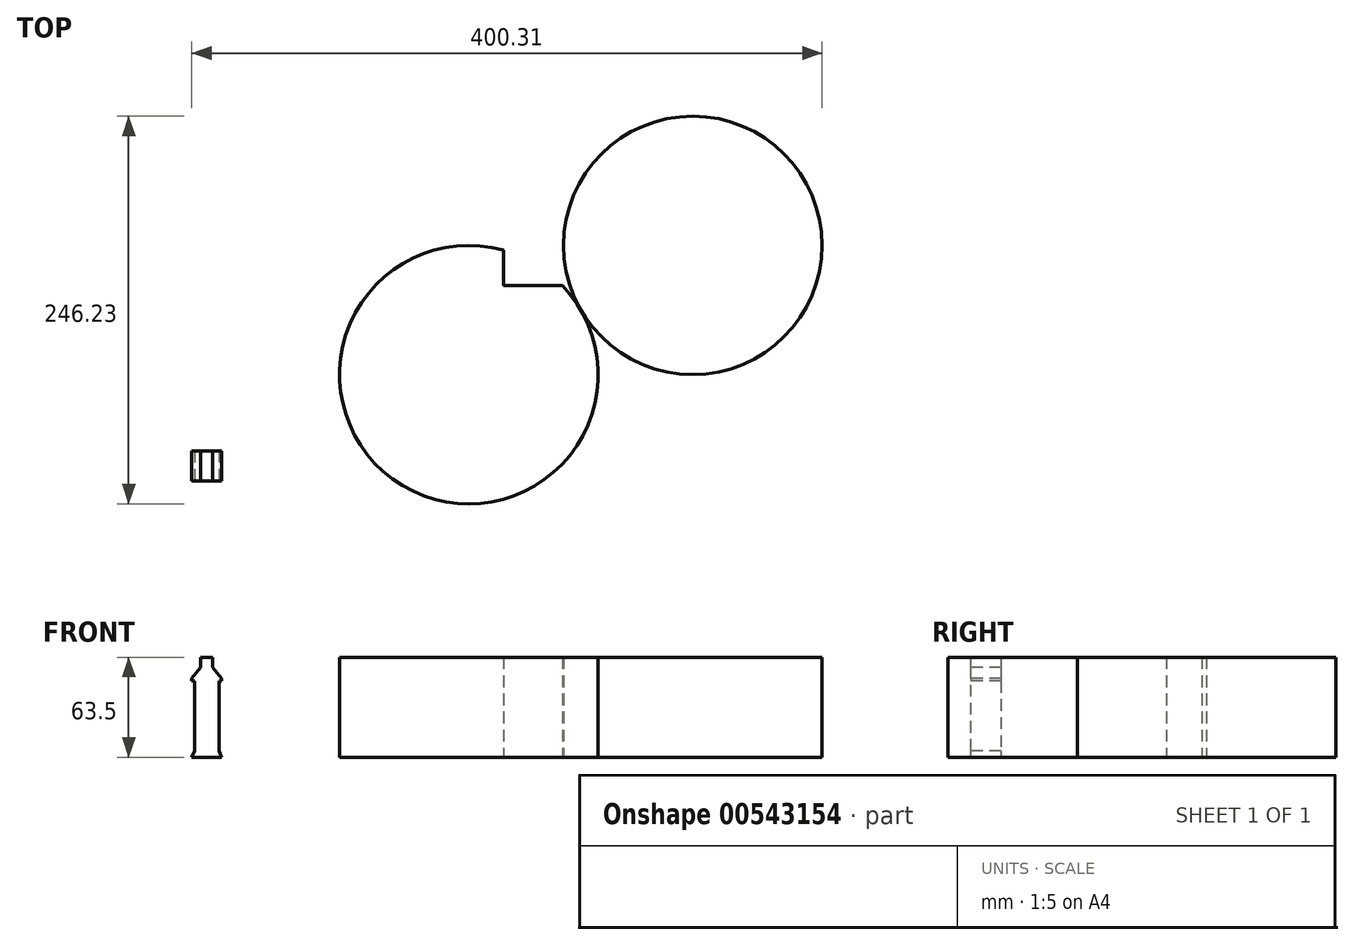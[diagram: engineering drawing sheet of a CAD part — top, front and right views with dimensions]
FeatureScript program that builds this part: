
annotation { "Feature Type Name" : "Feature", "Feature Type Description" : "" }
export const myFeature = defineFeature(function(context is Context, id is Id, definition is map)
    precondition{}
    {
        {
            var Q0;
            Q0=qCreatedBy(makeId("Top.planeOp"),FACE);
            var sketch = newSketch(context, id + "F0", { "sketchPlane" : qUnion([Q0])});
            skCircle(sketch, "E0", {"center": v(0, 0) * mm, "radius": 82.08 * mm});
            skCircle(sketch, "E1", {"center": v(0, 164.15) * mm, "radius": 82.08 * mm});
            skCircle(sketch, "E2", {"center": v(142.26, 82.08) * mm, "radius": 82.08 * mm});
            skPoint(sketch, "E3.startSnap0", {"position": v(71.13, 41.04) * mm});
            skLineSegment(sketch, "E4.bottom", {"start": v(21.96, 107.48) * mm, "end": v(72.76, 107.48) * mm});
            skLineSegment(sketch, "E4.top", {"start": v(21.96, 56.68) * mm, "end": v(72.76, 56.68) * mm});
            skLineSegment(sketch, "E4.left", {"start": v(21.96, 107.48) * mm, "end": v(21.96, 56.68) * mm});
            skLineSegment(sketch, "E4.right", {"start": v(72.76, 107.48) * mm, "end": v(72.76, 56.68) * mm});
            skSolve(sketch);
        }
        {
            var Q0;
            {var subQ0=sQuery(id+"F0.wireOp",EDGE,"E2");var subQ1=makeQuery(id+"F0.imprint","INTERSECT",VERTEX,{"derivedFrom":[sQuery(id+"F0.wireOp",EDGE,"5Xh8nU1x-Kccz-F1XJ-XfT3-ni66cKLijJze"),subQ0]});Q0=makeQuery(id+"F0.imprint","IMPRINT",FACE,{"disambiguationData":[TD([[makeQuery(id+"F0.imprint","IMPRINT",EDGE,{"disambiguationData":[TD([[subQ1,1.0]])],"derivedFrom":subQ0}),1.0]])]});}
            var Q1;
            {var subQ0=sQuery(id+"F0.wireOp",EDGE,"rKZXuCPi-gWcS-8Nuf-9jpB-Da6s8gIS6jwx");var subQ3=sQuery(id+"F0.wireOp",EDGE,"E2");var subQ7=makeQuery(id+"F0.imprint","INTERSECT",VERTEX,{"derivedFrom":[subQ3,subQ0]});Q1=makeQuery(id+"F0.imprint","IMPRINT",FACE,{"disambiguationData":[TD([[makeQuery(id+"F0.imprint","IMPRINT",EDGE,{"disambiguationData":[TD([[subQ7,-1.0]])],"derivedFrom":subQ3}),1.0]])]});}
            var Q2;
            {var subQ0=sQuery(id+"F0.wireOp",EDGE,"gLqf2wn5-t1Jo-fTFw-Qeks-cKj9YftUuhbS");var subQ1=sQuery(id+"F0.wireOp",EDGE,"E2");var subQ3=makeQuery(id+"F0.imprint","INTERSECT",VERTEX,{"derivedFrom":[subQ1,subQ0]});Q2=makeQuery(id+"F0.imprint","IMPRINT",FACE,{"disambiguationData":[TD([[makeQuery(id+"F0.imprint","IMPRINT",EDGE,{"disambiguationData":[TD([[subQ3,-1.0]])],"derivedFrom":subQ1}),1.0]])]});}
            var Q3;
            {var subQ0=sQuery(id+"F0.wireOp",EDGE,"ui8SPNsS-ngPU-wNeO-te97-4uBNf3wigOtR");Q3=makeQuery(id+"F0.imprint","IMPRINT",FACE,{"disambiguationData":[TD([[makeQuery(id+"F0.imprint","IMPRINT",EDGE,{"derivedFrom":subQ0}),1.0]])]});}
            var Q4;
            {var subQ0=sQuery(id+"F0.wireOp",EDGE,"ui8SPNsS-ngPU-wNeO-te97-4uBNf3wigOtR");Q4=makeQuery(id+"F0.imprint","IMPRINT",FACE,{"disambiguationData":[TD([[makeQuery(id+"F0.imprint","IMPRINT",EDGE,{"derivedFrom":subQ0}),-1.0]])]});}
            var Q5;
            {var subQ0=sQuery(id+"F0.wireOp",EDGE,"4fa8Zo42-phiU-RVQB-DN5M-7mljlmKBfd5X");Q5=makeQuery(id+"F0.imprint","IMPRINT",FACE,{"disambiguationData":[TD([[makeQuery(id+"F0.imprint","IMPRINT",EDGE,{"derivedFrom":subQ0}),-1.0]])]});}
            var Q6;
            {var subQ0=sQuery(id+"F0.wireOp",EDGE,"E3");var subQ1=sQuery(id+"F0.wireOp",EDGE,"E0");var subQ3=makeQuery(id+"F0.imprint","INTERSECT",VERTEX,{"derivedFrom":[subQ1,subQ0]});Q6=makeQuery(id+"F0.imprint","IMPRINT",FACE,{"disambiguationData":[TD([[makeQuery(id+"F0.imprint","IMPRINT",EDGE,{"disambiguationData":[TD([[subQ3,-1.0]])],"derivedFrom":subQ1}),1.0]])]});}
            var Q7;
            {var subQ0=sQuery(id+"F0.wireOp",EDGE,"HXteInfV-cd6M-VXyz-XBM5-8RgosEx2xvVP");Q7=makeQuery(id+"F0.imprint","IMPRINT",FACE,{"disambiguationData":[TD([[makeQuery(id+"F0.imprint","IMPRINT",EDGE,{"derivedFrom":subQ0}),1.0]])]});}
            var Q8;
            {var subQ5=sQuery(id+"F0.wireOp",EDGE,"HXteInfV-cd6M-VXyz-XBM5-8RgosEx2xvVP");Q8=makeQuery(id+"F0.imprint","IMPRINT",FACE,{"disambiguationData":[TD([[makeQuery(id+"F0.imprint","IMPRINT",EDGE,{"derivedFrom":subQ5}),-1.0]])]});}
            var Q9;
            {var subQ0=sQuery(id+"F0.wireOp",EDGE,"5Xh8nU1x-Kccz-F1XJ-XfT3-ni66cKLijJze");var subQ1=sQuery(id+"F0.wireOp",EDGE,"E0");var subQ2=makeQuery(id+"F0.imprint","INTERSECT",VERTEX,{"derivedFrom":[subQ1,subQ0]});Q9=makeQuery(id+"F0.imprint","IMPRINT",FACE,{"disambiguationData":[TD([[makeQuery(id+"F0.imprint","IMPRINT",EDGE,{"disambiguationData":[TD([[subQ2,-1.0]])],"derivedFrom":subQ1}),1.0]])]});}
            extrude(context, id + "F1", {"entities" : qUnion([Q0, Q1, Q2, Q3, Q4, Q5, Q6, Q7, Q8, Q9]), "depth" : 63.5 * mm, "offsetDistance" : 25.4 * mm});
        }
        {
            var Q0;
            Q0=qCreatedBy(makeId("Top.planeOp"),FACE);
            var sketch = newSketch(context, id + "F2", { "sketchPlane" : qUnion([Q0])});
            skLineSegment(sketch, "E5.bottom", {"start": v(-175.97, -48.4) * mm, "end": v(-156.92, -48.4) * mm});
            skLineSegment(sketch, "E5.top", {"start": v(-175.97, -67.45) * mm, "end": v(-156.92, -67.45) * mm});
            skLineSegment(sketch, "E5.left", {"start": v(-175.97, -48.4) * mm, "end": v(-175.97, -67.45) * mm});
            skLineSegment(sketch, "E5.right", {"start": v(-156.92, -48.4) * mm, "end": v(-156.92, -67.45) * mm});
            skSolve(sketch);
        }
        {
            var Q0;
            Q0=makeQuery(id+"F2.imprint","IMPRINT",FACE,{"disambiguationData":[TD([[makeQuery(id+"F2.imprint","IMPRINT",EDGE,{"derivedFrom":sQuery(id+"F2.wireOp",EDGE,"E5.bottom")}),-1.0]])]});
            extrude(context, id + "F3", {"entities" : qUnion([Q0]), "depth" : 63.5 * mm, "offsetDistance" : 25.4 * mm});
        }
        {
            var Q0;
            Q0=makeQuery(id+"F3.opExtrude","SWEPT_FACE",FACE,{"disambiguationData":[OSD([sQuery(id+"F2.wireOp",EDGE,"E5.top")])]});
            var sketch = newSketch(context, id + "F4", { "sketchPlane" : qUnion([Q0])});
            skLineSegment(sketch, "E6", {"start": v(-156.92, 0) * mm, "end": v(-158.7, 4.1) * mm});
            skLineSegment(sketch, "E7", {"start": v(-158.7, 4.1) * mm, "end": v(-158.7, 48.5) * mm});
            skLineSegment(sketch, "E8", {"start": v(-158.7, 48.5) * mm, "end": v(-156.92, 48.5) * mm});
            skLineSegment(sketch, "E9", {"start": v(-156.92, 48.5) * mm, "end": v(-156.92, 50.05) * mm});
            skLineSegment(sketch, "E10", {"start": v(-156.92, 50.05) * mm, "end": v(-162.65, 57.18) * mm});
            skLineSegment(sketch, "E11", {"start": v(-162.65, 57.18) * mm, "end": v(-162.65, 63.5) * mm});
            skLineSegment(sketch, "E12", {"start": v(-166.44, 63.5) * mm, "end": v(-166.44, 0) * mm});
            skLineSegment(sketch, "E13.MirrorCS", {"start": v(-175.97, 0) * mm, "end": v(-174.18, 4.1) * mm});
            skLineSegment(sketch, "E14.MirrorCS", {"start": v(-174.18, 4.1) * mm, "end": v(-174.18, 48.5) * mm});
            skLineSegment(sketch, "E15.MirrorCS", {"start": v(-174.18, 48.5) * mm, "end": v(-175.97, 48.5) * mm});
            skLineSegment(sketch, "E16.MirrorCS", {"start": v(-175.97, 48.5) * mm, "end": v(-175.97, 50.05) * mm});
            skLineSegment(sketch, "E17.MirrorCS", {"start": v(-170.23, 57.18) * mm, "end": v(-170.23, 63.5) * mm});
            skLineSegment(sketch, "E18.MirrorCS", {"start": v(-175.97, 50.05) * mm, "end": v(-170.23, 57.18) * mm});
            skSolve(sketch);
        }
        {
            var Q0;
            {var subQ0=sQuery(id+"F4.wireOp",EDGE,"E10");Q0=makeQuery(id+"F4.imprint","IMPRINT",FACE,{"disambiguationData":[TD([[makeQuery(id+"F4.imprint","IMPRINT",EDGE,{"derivedFrom":subQ0}),-1.0]])]});}
            var Q1;
            {var subQ0=sQuery(id+"F4.wireOp",EDGE,"E6");Q1=makeQuery(id+"F4.imprint","IMPRINT",FACE,{"disambiguationData":[TD([[makeQuery(id+"F4.imprint","IMPRINT",EDGE,{"derivedFrom":subQ0}),-1.0]])]});}
            extrude(context, id + "F5", {"entities" : qUnion([Q0, Q1]), "operationType" : NewBodyOperationType.REMOVE, "oppositeDirection" : true, "depth" : 25.4 * mm, "offsetDistance" : 25.4 * mm});
        }
        {
            var Q0;
            {var subQ0=sQuery(id+"F4.wireOp",EDGE,"E17.MirrorCS");Q0=makeQuery(id+"F4.imprint","IMPRINT",FACE,{"disambiguationData":[TD([[makeQuery(id+"F4.imprint","IMPRINT",EDGE,{"derivedFrom":subQ0}),1.0]])]});}
            var Q1;
            {var subQ0=sQuery(id+"F4.wireOp",EDGE,"E13.MirrorCS");Q1=makeQuery(id+"F4.imprint","IMPRINT",FACE,{"disambiguationData":[TD([[makeQuery(id+"F4.imprint","IMPRINT",EDGE,{"derivedFrom":subQ0}),1.0]])]});}
            extrude(context, id + "F6", {"entities" : qUnion([Q0, Q1]), "operationType" : NewBodyOperationType.REMOVE, "oppositeDirection" : true, "depth" : 25.4 * mm, "offsetDistance" : 25.4 * mm});
        }
    });
